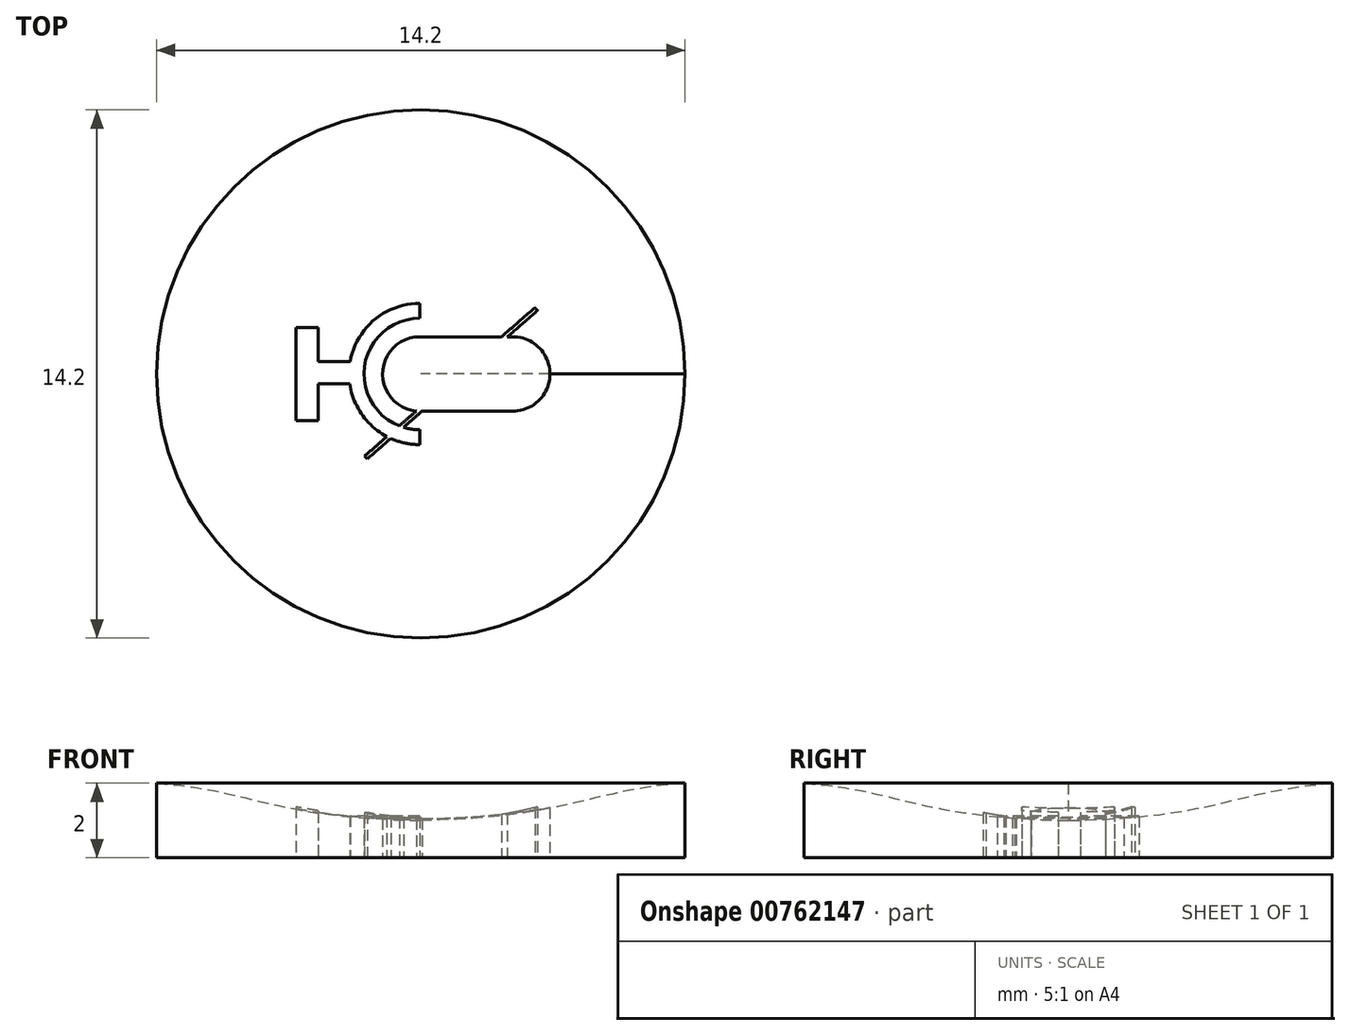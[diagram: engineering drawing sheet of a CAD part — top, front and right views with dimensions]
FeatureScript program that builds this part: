
annotation { "Feature Type Name" : "Feature", "Feature Type Description" : "" }
export const myFeature = defineFeature(function(context is Context, id is Id, definition is map)
    precondition{}
    {
        {
            var Q0;
            Q0=qCreatedBy(makeId("Front.planeOp"),FACE);
            var sketch = newSketch(context, id + "F0", { "sketchPlane" : qUnion([Q0])});
            skLineSegment(sketch, "E0", {"start": v(0, 0) * mm, "end": v(7.1, 0) * mm});
            skLineSegment(sketch, "E1", {"start": v(7.1, 0) * mm, "end": v(7.1, 2) * mm});
            skLineSegment(sketch, "E2", {"start": v(0, 1) * mm, "end": v(0, 0) * mm});
            skFitSpline(sketch, "E3", {"points": [v(7.1, 2) * mm, v(0, 1) * mm], "startDerivative": vector(-7.89, -0.57) * mm, "endDerivative": vector(-12, -0.18) * mm});
            skPoint(sketch, "E4.orphan", {"position": v(0, 2) * mm});
            skSolve(sketch);
        }
        {
            var Q0;
            Q0=makeQuery(id+"F0.imprint","IMPRINT",FACE,{"disambiguationData":[TD([[makeQuery(id+"F0.imprint","IMPRINT",EDGE,{"derivedFrom":sQuery(id+"F0.wireOp",EDGE,"E0")}),1.0]])]});
            var Q1;
            Q1=sQuery(id+"F0.wireOp",EDGE,"E2");
            revolve(context, id + "F1", {"entities" : qUnion([Q0]), "axis" : qUnion([Q1]), "revolveType" : RevolveType.FULL, "surfaceOperationType" : NewSurfaceOperationType.NEW});
        }
        {
            var Q0;
            Q0=makeQuery(id+"F1.opRevolve","SWEPT_FACE",FACE,{"disambiguationData":[OSD([sQuery(id+"F0.wireOp",EDGE,"E0")])]});
            var sketch = newSketch(context, id + "F2", { "sketchPlane" : qUnion([Q0])});
            skLineSegment(sketch, "E5.bottom", {"start": v(2.47, 1) * mm, "end": v(0.04, 1) * mm});
            skLineSegment(sketch, "E5.top", {"start": v(2.47, -1) * mm, "end": v(2.33, -1) * mm});
            skArc(sketch, "E6", {"start": v(-0.12, 1) * mm, "mid": v(-1.03, -0.05) * mm, "end": v(-0.03, -1) * mm});
            skArc(sketch, "E7", {"start": v(2.47, -1) * mm, "mid": v(3.47, 0) * mm, "end": v(2.47, 1) * mm});
            skArc(sketch, "E8", {"start": v(-0.03, 1.5) * mm, "mid": v(-0.25, 1.48) * mm, "end": v(-0.46, 1.44) * mm});
            skArc(sketch, "E9.0", {"start": v(-0.03, 1.9) * mm, "mid": v(-0.42, 1.86) * mm, "end": v(-0.8, 1.73) * mm});
            skLineSegment(sketch, "E10", {"start": v(-0.03, -1.9) * mm, "end": v(-0.03, -1.5) * mm});
            skLineSegment(sketch, "E11.trimOffspring", {"start": v(-0.03, 1.5) * mm, "end": v(-0.03, 1.9) * mm});
            skLineSegment(sketch, "E12.bottom", {"start": v(-1.9, 0.27) * mm, "end": v(-2.75, 0.27) * mm});
            skLineSegment(sketch, "E12.top", {"start": v(-1.9, -0.33) * mm, "end": v(-2.75, -0.33) * mm});
            skLineSegment(sketch, "E13.bottom", {"start": v(-3.35, 1.25) * mm, "end": v(-2.75, 1.25) * mm});
            skLineSegment(sketch, "E13.top", {"start": v(-3.35, -1.25) * mm, "end": v(-2.75, -1.25) * mm});
            skLineSegment(sketch, "E13.left", {"start": v(-3.35, 1.25) * mm, "end": v(-3.35, -1.25) * mm});
            skLineSegment(sketch, "E13.right", {"start": v(-2.75, 1.25) * mm, "end": v(-2.75, 0.27) * mm});
            skLineSegment(sketch, "E14.trimOffspring", {"start": v(-2.75, -0.33) * mm, "end": v(-2.75, -1.25) * mm});
            skArc(sketch, "E15.trimOffspring", {"start": v(-1.9, -0.33) * mm, "mid": v(-1.25, -1.46) * mm, "end": v(-0.03, -1.9) * mm});
            skLineSegment(sketch, "E16", {"start": v(-1.95, -0.33) * mm, "end": v(-1.9, -0.33) * mm});
            skLineSegment(sketch, "E17", {"start": v(-1.43, 2.28) * mm, "end": v(-0.8, 1.73) * mm});
            skLineSegment(sketch, "E18", {"start": v(3.14, -1.7) * mm, "end": v(3.07, -1.78) * mm});
            skLineSegment(sketch, "E19", {"start": v(3.07, -1.78) * mm, "end": v(2.17, -1) * mm});
            skLineSegment(sketch, "E20", {"start": v(-1.5, 2.2) * mm, "end": v(-1.43, 2.28) * mm});
            skLineSegment(sketch, "E21.trimOffspring", {"start": v(-0.12, 1) * mm, "end": v(-0.58, 1.4) * mm});
            skLineSegment(sketch, "E22.trimOffspring", {"start": v(2.33, -1) * mm, "end": v(3.14, -1.7) * mm});
            skLineSegment(sketch, "E23.trimOffspring", {"start": v(-0.46, 1.44) * mm, "end": v(0.04, 1) * mm});
            skLineSegment(sketch, "E24.trimOffspring", {"start": v(-0.9, 1.68) * mm, "end": v(-1.5, 2.2) * mm});
            skArc(sketch, "E25.trimOffspring", {"start": v(-0.58, 1.4) * mm, "mid": v(-1.5, -0.28) * mm, "end": v(-0.03, -1.5) * mm});
            skArc(sketch, "E26.trimOffspring", {"start": v(-0.9, 1.68) * mm, "mid": v(-1.58, 1.1) * mm, "end": v(-1.9, 0.27) * mm});
            skLineSegment(sketch, "E27.trimOffspring", {"start": v(2.17, -1) * mm, "end": v(-0.03, -1) * mm});
            skSolve(sketch);
        }
        {
            var Q0;
            Q0=makeQuery(id+"F2.imprint","IMPRINT",FACE,{"disambiguationData":[TD([[makeQuery(id+"F2.imprint","IMPRINT",EDGE,{"derivedFrom":sQuery(id+"F2.wireOp",EDGE,"E5.bottom")}),1.0]])]});
            extrude(context, id + "F3", {"entities" : qUnion([Q0]), "endBound" : BoundingType.UP_TO_NEXT, "oppositeDirection" : true, "depth" : 25 * mm, "hasOffset" : true, "offsetDistance" : 0.02 * mm, "offsetOppositeDirection" : true});
        }
    });
